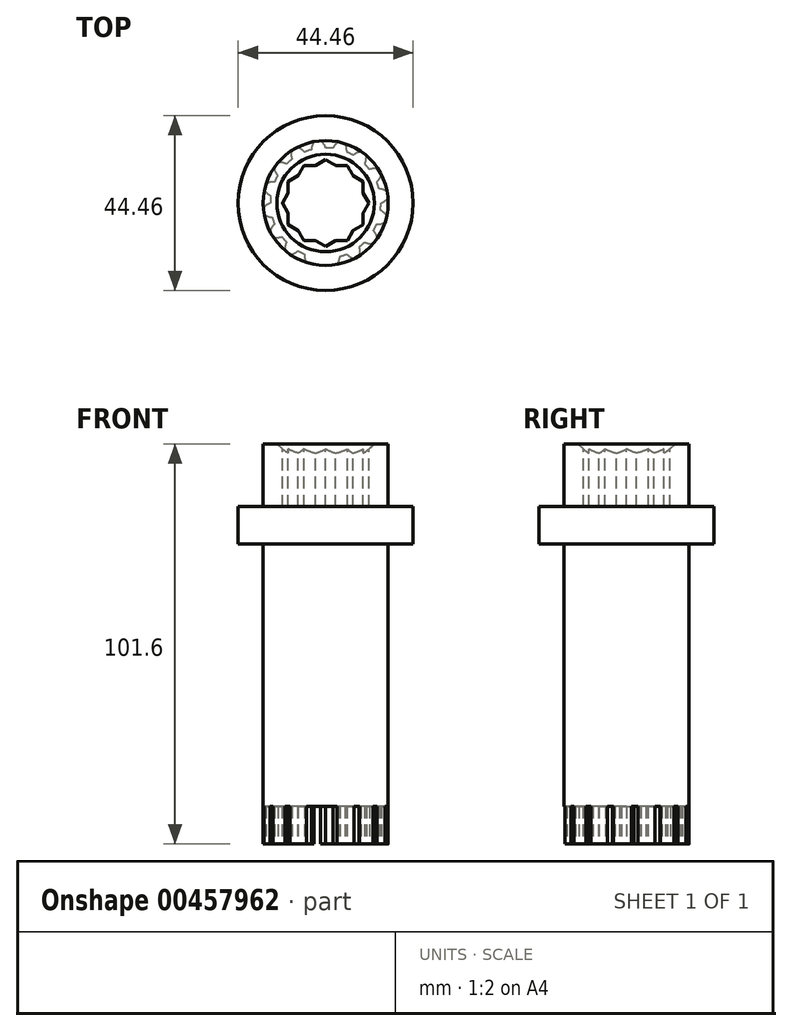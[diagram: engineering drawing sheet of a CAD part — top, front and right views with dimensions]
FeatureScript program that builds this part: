
annotation { "Feature Type Name" : "Feature", "Feature Type Description" : "" }
export const myFeature = defineFeature(function(context is Context, id is Id, definition is map)
    precondition{}
    {
        {
            var Q0;
            Q0=qCreatedBy(makeId("Front.planeOp"),FACE);
            var sketch = newSketch(context, id + "F0", { "sketchPlane" : qUnion([Q0])});
            skLineSegment(sketch, "E0", {"start": v(0, 0) * mm, "end": v(0, 64.52) * mm, "construction": true});
            skLineSegment(sketch, "E1", {"start": v(0, 101.6) * mm, "end": v(-15.88, 101.6) * mm});
            skLineSegment(sketch, "E2", {"start": v(-15.88, 101.6) * mm, "end": v(-15.88, 0) * mm});
            skLineSegment(sketch, "E3", {"start": v(-15.88, 0) * mm, "end": v(0, 0) * mm});
            skLineSegment(sketch, "E4", {"start": v(0, 101.6) * mm, "end": v(0, 0) * mm});
            skSolve(sketch);
        }
        {
            var Q0;
            Q0=qSketchRegion(id+"F0",true);
            var Q1;
            Q1=sQuery(id+"F0.wireOp",EDGE,"E4");
            revolve(context, id + "F1", {"entities" : qUnion([Q0]), "axis" : qUnion([Q1]), "revolveType" : RevolveType.FULL});
        }
        {
            var Q0;
            Q0=makeQuery(id+"F1.opRevolve","SWEPT_FACE",FACE,{"disambiguationData":[OSD([sQuery(id+"F0.wireOp",EDGE,"E3")])]});
            var sketch = newSketch(context, id + "F2", { "sketchPlane" : qUnion([Q0])});
            skCircle(sketch, "E5", {"center": v(0, 0) * mm, "radius": 15.87 * mm, "construction": true});
            skCircle(sketch, "E6", {"center": v(0, 0) * mm, "radius": 13.25 * mm, "construction": true});
            skCircle(sketch, "E7", {"center": v(0, 0) * mm, "radius": 14.03 * mm, "construction": true});
            skArc(sketch, "E8", {"start": v(1.24, 15.83) * mm, "mid": v(0.49, 15.02) * mm, "end": v(0, 14.03) * mm});
            skLineSegment(sketch, "E9", {"start": v(0, 14.03) * mm, "end": v(0, 17.07) * mm, "construction": true});
            skLineSegment(sketch, "E10", {"start": v(0, 0) * mm, "end": v(-1.3, 19.98) * mm, "construction": true});
            skArc(sketch, "E11.MirrorCS", {"start": v(-3.3, 15.53) * mm, "mid": v(-2.45, 14.83) * mm, "end": v(-1.83, 13.9) * mm});
            skArc(sketch, "E12", {"start": v(0, 14.03) * mm, "mid": v(-0.92, 14) * mm, "end": v(-1.83, 13.9) * mm});
            skArc(sketch, "E13.1.0", {"start": v(-8.99, 13.09) * mm, "mid": v(-7.93, 12.76) * mm, "end": v(-7.01, 12.15) * mm});
            skArc(sketch, "E13.1.2", {"start": v(-4.9, 15.1) * mm, "mid": v(-5.3, 14.06) * mm, "end": v(-5.37, 12.96) * mm});
            skArc(sketch, "E13.1.3", {"start": v(-5.37, 12.96) * mm, "mid": v(-6.2, 12.59) * mm, "end": v(-7.01, 12.15) * mm});
            skArc(sketch, "E13.2.0", {"start": v(-13.31, 8.65) * mm, "mid": v(-12.21, 8.75) * mm, "end": v(-11.13, 8.54) * mm});
            skArc(sketch, "E13.2.1", {"start": v(-10.31, 12.07) * mm, "mid": v(-12.13, 10.64) * mm, "end": v(-13.31, 8.65) * mm});
            skArc(sketch, "E13.2.2", {"start": v(-10.31, 12.07) * mm, "mid": v(-10.27, 10.97) * mm, "end": v(-9.92, 9.92) * mm});
            skArc(sketch, "E13.2.3", {"start": v(-9.92, 9.92) * mm, "mid": v(-10.55, 9.25) * mm, "end": v(-11.13, 8.54) * mm});
            skArc(sketch, "E13.3.0", {"start": v(-15.6, 2.9) * mm, "mid": v(-14.63, 3.41) * mm, "end": v(-13.55, 3.63) * mm});
            skArc(sketch, "E13.3.2", {"start": v(-14.15, 7.2) * mm, "mid": v(-13.69, 6.2) * mm, "end": v(-12.96, 5.37) * mm});
            skArc(sketch, "E13.3.3", {"start": v(-12.96, 5.37) * mm, "mid": v(-13.3, 4.51) * mm, "end": v(-13.55, 3.63) * mm});
            skArc(sketch, "E13.4.0", {"start": v(-15.53, -3.3) * mm, "mid": v(-14.83, -2.45) * mm, "end": v(-13.9, -1.83) * mm});
            skArc(sketch, "E13.4.2", {"start": v(-15.83, 1.24) * mm, "mid": v(-15.02, 0.49) * mm, "end": v(-14.03, 0) * mm});
            skArc(sketch, "E13.4.3", {"start": v(-14.03, 0) * mm, "mid": v(-14, -0.92) * mm, "end": v(-13.9, -1.83) * mm});
            skArc(sketch, "E13.5.0", {"start": v(-13.09, -8.99) * mm, "mid": v(-12.76, -7.93) * mm, "end": v(-12.15, -7.01) * mm});
            skArc(sketch, "E13.5.2", {"start": v(-15.1, -4.9) * mm, "mid": v(-14.06, -5.3) * mm, "end": v(-12.96, -5.37) * mm});
            skArc(sketch, "E13.5.3", {"start": v(-12.96, -5.37) * mm, "mid": v(-12.59, -6.2) * mm, "end": v(-12.15, -7.01) * mm});
            skArc(sketch, "E13.6.0", {"start": v(-8.65, -13.31) * mm, "mid": v(-8.75, -12.21) * mm, "end": v(-8.54, -11.13) * mm});
            skArc(sketch, "E13.6.2", {"start": v(-12.07, -10.31) * mm, "mid": v(-10.97, -10.27) * mm, "end": v(-9.92, -9.92) * mm});
            skArc(sketch, "E13.6.3", {"start": v(-9.92, -9.92) * mm, "mid": v(-9.25, -10.55) * mm, "end": v(-8.54, -11.13) * mm});
            skArc(sketch, "E13.7.0", {"start": v(-2.9, -15.6) * mm, "mid": v(-3.41, -14.63) * mm, "end": v(-3.63, -13.55) * mm});
            skArc(sketch, "E13.7.2", {"start": v(-7.2, -14.15) * mm, "mid": v(-6.2, -13.69) * mm, "end": v(-5.37, -12.96) * mm});
            skArc(sketch, "E13.7.3", {"start": v(-5.37, -12.96) * mm, "mid": v(-4.51, -13.3) * mm, "end": v(-3.63, -13.55) * mm});
            skArc(sketch, "E13.8.0", {"start": v(3.3, -15.53) * mm, "mid": v(2.45, -14.83) * mm, "end": v(1.83, -13.9) * mm});
            skArc(sketch, "E13.8.2", {"start": v(-1.24, -15.83) * mm, "mid": v(-0.49, -15.02) * mm, "end": v(0, -14.03) * mm});
            skArc(sketch, "E13.8.3", {"start": v(0, -14.03) * mm, "mid": v(0.92, -14) * mm, "end": v(1.83, -13.9) * mm});
            skArc(sketch, "E13.9.0", {"start": v(8.99, -13.09) * mm, "mid": v(7.93, -12.76) * mm, "end": v(7.01, -12.15) * mm});
            skArc(sketch, "E13.9.2", {"start": v(4.9, -15.1) * mm, "mid": v(5.3, -14.06) * mm, "end": v(5.37, -12.96) * mm});
            skArc(sketch, "E13.9.3", {"start": v(5.37, -12.96) * mm, "mid": v(6.2, -12.59) * mm, "end": v(7.01, -12.15) * mm});
            skArc(sketch, "E13.10.0", {"start": v(13.31, -8.65) * mm, "mid": v(12.21, -8.75) * mm, "end": v(11.13, -8.54) * mm});
            skArc(sketch, "E13.10.2", {"start": v(10.31, -12.07) * mm, "mid": v(10.27, -10.97) * mm, "end": v(9.92, -9.92) * mm});
            skArc(sketch, "E13.10.3", {"start": v(9.92, -9.92) * mm, "mid": v(10.55, -9.25) * mm, "end": v(11.13, -8.54) * mm});
            skArc(sketch, "E13.11.0", {"start": v(15.6, -2.9) * mm, "mid": v(14.63, -3.41) * mm, "end": v(13.55, -3.63) * mm});
            skArc(sketch, "E13.11.2", {"start": v(14.15, -7.2) * mm, "mid": v(13.69, -6.2) * mm, "end": v(12.96, -5.37) * mm});
            skArc(sketch, "E13.11.3", {"start": v(12.96, -5.37) * mm, "mid": v(13.3, -4.51) * mm, "end": v(13.55, -3.63) * mm});
            skArc(sketch, "E13.12.0", {"start": v(15.53, 3.3) * mm, "mid": v(14.83, 2.45) * mm, "end": v(13.9, 1.83) * mm});
            skArc(sketch, "E13.12.2", {"start": v(15.83, -1.24) * mm, "mid": v(15.02, -0.49) * mm, "end": v(14.03, 0) * mm});
            skArc(sketch, "E13.12.3", {"start": v(14.03, 0) * mm, "mid": v(14, 0.92) * mm, "end": v(13.9, 1.83) * mm});
            skArc(sketch, "E13.13.0", {"start": v(13.09, 8.99) * mm, "mid": v(12.76, 7.93) * mm, "end": v(12.15, 7.01) * mm});
            skArc(sketch, "E13.13.2", {"start": v(15.1, 4.9) * mm, "mid": v(14.06, 5.3) * mm, "end": v(12.96, 5.37) * mm});
            skArc(sketch, "E13.13.3", {"start": v(12.96, 5.37) * mm, "mid": v(12.59, 6.2) * mm, "end": v(12.15, 7.01) * mm});
            skArc(sketch, "E13.14.0", {"start": v(8.65, 13.31) * mm, "mid": v(8.75, 12.21) * mm, "end": v(8.54, 11.13) * mm});
            skArc(sketch, "E13.14.2", {"start": v(12.07, 10.31) * mm, "mid": v(10.97, 10.27) * mm, "end": v(9.92, 9.92) * mm});
            skArc(sketch, "E13.14.3", {"start": v(9.92, 9.92) * mm, "mid": v(9.25, 10.55) * mm, "end": v(8.54, 11.13) * mm});
            skArc(sketch, "E13.15.0", {"start": v(2.9, 15.6) * mm, "mid": v(3.41, 14.63) * mm, "end": v(3.63, 13.55) * mm});
            skArc(sketch, "E13.15.2", {"start": v(7.2, 14.15) * mm, "mid": v(6.2, 13.69) * mm, "end": v(5.37, 12.96) * mm});
            skArc(sketch, "E13.15.3", {"start": v(5.37, 12.96) * mm, "mid": v(4.51, 13.3) * mm, "end": v(3.63, 13.55) * mm});
            skCircle(sketch, "E14", {"center": v(0, 0) * mm, "radius": 18.28 * mm});
            skSolve(sketch);
        }
        {
            var Q0;
            Q0=makeQuery(id+"F1.opRevolve","SWEPT_FACE",FACE,{"disambiguationData":[OSD([sQuery(id+"F0.wireOp",EDGE,"E1")])]});
            var sketch = newSketch(context, id + "F3", { "sketchPlane" : qUnion([Q0])});
            skCircle(sketch, "E15.cCircle", {"center": v(0, 0) * mm, "radius": 9.53 * mm, "construction": true});
            skLineSegment(sketch, "E15.0", {"start": v(-5.5, 9.53) * mm, "end": v(5.5, 9.53) * mm, "construction": true});
            skLineSegment(sketch, "E15.1", {"start": v(5.5, 9.52) * mm, "end": v(11, 0) * mm, "construction": true});
            skLineSegment(sketch, "E15.2", {"start": v(11, 0) * mm, "end": v(5.5, -9.52) * mm, "construction": true});
            skLineSegment(sketch, "E15.3", {"start": v(5.5, -9.52) * mm, "end": v(-5.5, -9.53) * mm, "construction": true});
            skLineSegment(sketch, "E15.4", {"start": v(-5.5, -9.53) * mm, "end": v(-11, 0) * mm, "construction": true});
            skLineSegment(sketch, "E15.5", {"start": v(-11, 0) * mm, "end": v(-5.5, 9.52) * mm, "construction": true});
            skPoint(sketch, "E15.0.midPoint", {"position": v(0, 9.53) * mm});
            skLineSegment(sketch, "E16.0", {"start": v(9.53, 5.5) * mm, "end": v(9.53, -5.5) * mm, "construction": true});
            skLineSegment(sketch, "E16.1", {"start": v(9.52, -5.5) * mm, "end": v(0, -11) * mm, "construction": true});
            skLineSegment(sketch, "E16.2", {"start": v(0, -11) * mm, "end": v(-9.52, -5.5) * mm, "construction": true});
            skLineSegment(sketch, "E16.3", {"start": v(-9.52, -5.5) * mm, "end": v(-9.53, 5.5) * mm, "construction": true});
            skLineSegment(sketch, "E16.4", {"start": v(-9.53, 5.5) * mm, "end": v(0, 11) * mm, "construction": true});
            skLineSegment(sketch, "E16.5", {"start": v(0, 11) * mm, "end": v(9.52, 5.5) * mm, "construction": true});
            skPoint(sketch, "E16.0.midPoint", {"position": v(9.53, 0) * mm});
            skLineSegment(sketch, "E17", {"start": v(-5.5, 9.53) * mm, "end": v(-2.55, 9.53) * mm});
            skLineSegment(sketch, "E18", {"start": v(-2.55, 9.53) * mm, "end": v(0, 11) * mm});
            skLineSegment(sketch, "E19", {"start": v(0, 11) * mm, "end": v(2.55, 9.53) * mm});
            skLineSegment(sketch, "E20", {"start": v(2.55, 9.53) * mm, "end": v(5.5, 9.53) * mm});
            skLineSegment(sketch, "E21", {"start": v(5.5, 9.53) * mm, "end": v(6.97, 6.97) * mm});
            skLineSegment(sketch, "E22", {"start": v(6.97, 6.97) * mm, "end": v(9.53, 5.5) * mm});
            skLineSegment(sketch, "E23", {"start": v(9.53, 2.55) * mm, "end": v(11, 0) * mm});
            skLineSegment(sketch, "E24", {"start": v(11, 0) * mm, "end": v(9.53, -2.55) * mm});
            skLineSegment(sketch, "E25", {"start": v(9.53, -2.55) * mm, "end": v(9.53, -5.5) * mm});
            skLineSegment(sketch, "E26", {"start": v(9.53, -5.5) * mm, "end": v(6.97, -6.97) * mm});
            skLineSegment(sketch, "E27", {"start": v(6.97, -6.97) * mm, "end": v(5.5, -9.52) * mm});
            skLineSegment(sketch, "E28", {"start": v(2.55, -9.53) * mm, "end": v(0, -11) * mm});
            skLineSegment(sketch, "E29", {"start": v(-2.55, -9.53) * mm, "end": v(-5.5, -9.53) * mm});
            skLineSegment(sketch, "E30", {"start": v(-6.97, -6.97) * mm, "end": v(-9.52, -5.5) * mm});
            skLineSegment(sketch, "E31", {"start": v(-9.53, -2.55) * mm, "end": v(-11, 0) * mm});
            skLineSegment(sketch, "E32", {"start": v(-9.52, -5.5) * mm, "end": v(-9.53, -2.55) * mm});
            skLineSegment(sketch, "E33", {"start": v(-5.5, -9.53) * mm, "end": v(-6.97, -6.97) * mm});
            skLineSegment(sketch, "E34", {"start": v(0, -11) * mm, "end": v(-2.55, -9.53) * mm});
            skLineSegment(sketch, "E35", {"start": v(5.5, -9.52) * mm, "end": v(2.55, -9.53) * mm});
            skLineSegment(sketch, "E36", {"start": v(9.53, 5.5) * mm, "end": v(9.53, 2.55) * mm});
            skLineSegment(sketch, "E37", {"start": v(-5.5, 9.53) * mm, "end": v(-6.97, 6.97) * mm});
            skLineSegment(sketch, "E38", {"start": v(-6.97, 6.97) * mm, "end": v(-9.53, 5.5) * mm});
            skLineSegment(sketch, "E39", {"start": v(-9.53, 5.5) * mm, "end": v(-9.53, 2.55) * mm});
            skLineSegment(sketch, "E40", {"start": v(-9.53, 2.55) * mm, "end": v(-11, 0) * mm});
            skSolve(sketch);
        }
        {
            var Q0;
            Q0=qSketchRegion(id+"F3",true);
            extrude(context, id + "F4", {"entities" : qUnion([Q0]), "operationType" : NewBodyOperationType.REMOVE, "oppositeDirection" : true, "depth" : 19.05 * mm});
        }
        {
            var Q0;
            Q0=qCreatedBy(makeId("Front.planeOp"),FACE);
            var sketch = newSketch(context, id + "F5", { "sketchPlane" : qUnion([Q0])});
            skLineSegment(sketch, "E41", {"start": v(-15.88, 104.78) * mm, "end": v(-8.9, 98.43) * mm});
            skLineSegment(sketch, "E42", {"start": v(-8.9, 98.43) * mm, "end": v(0, 98.43) * mm});
            skLineSegment(sketch, "E43", {"start": v(0, 98.43) * mm, "end": v(0, 104.78) * mm});
            skLineSegment(sketch, "E44", {"start": v(0, 104.78) * mm, "end": v(-15.88, 104.78) * mm});
            skSolve(sketch);
        }
        {
            var Q0;
            Q0=qSketchRegion(id+"F5",true);
            var Q1;
            Q1=sQuery(id+"F5.wireOp",EDGE,"E43");
            revolve(context, id + "F6", {"operationType" : NewBodyOperationType.REMOVE, "entities" : qUnion([Q0]), "axis" : qUnion([Q1]), "revolveType" : RevolveType.FULL, "oppositeDirection" : true});
        }
        {
            var Q0;
            {var subQ0=sQuery(id+"F2.wireOp",EDGE,"E8");Q0=makeQuery(id+"F2.imprint","IMPRINT",FACE,{"disambiguationData":[TD([[makeQuery(id+"F2.imprint","IMPRINT",EDGE,{"derivedFrom":subQ0}),-1.0]])]});}
            var Q1;
            {var subQ0=sQuery(id+"F2.wireOp",EDGE,"E13.1.0");Q1=makeQuery(id+"F2.imprint","IMPRINT",FACE,{"disambiguationData":[TD([[makeQuery(id+"F2.imprint","IMPRINT",EDGE,{"derivedFrom":subQ0}),1.0]])]});}
            var Q2;
            {var subQ0=sQuery(id+"F2.wireOp",EDGE,"E13.2.0");Q2=makeQuery(id+"F2.imprint","IMPRINT",FACE,{"disambiguationData":[TD([[makeQuery(id+"F2.imprint","IMPRINT",EDGE,{"derivedFrom":subQ0}),1.0]])]});}
            var Q3;
            {var subQ0=sQuery(id+"F2.wireOp",EDGE,"E13.3.0");Q3=makeQuery(id+"F2.imprint","IMPRINT",FACE,{"disambiguationData":[TD([[makeQuery(id+"F2.imprint","IMPRINT",EDGE,{"derivedFrom":subQ0}),1.0]])]});}
            var Q4;
            {var subQ0=sQuery(id+"F2.wireOp",EDGE,"E13.4.0");Q4=makeQuery(id+"F2.imprint","IMPRINT",FACE,{"disambiguationData":[TD([[makeQuery(id+"F2.imprint","IMPRINT",EDGE,{"derivedFrom":subQ0}),1.0]])]});}
            var Q5;
            {var subQ0=sQuery(id+"F2.wireOp",EDGE,"E13.5.0");Q5=makeQuery(id+"F2.imprint","IMPRINT",FACE,{"disambiguationData":[TD([[makeQuery(id+"F2.imprint","IMPRINT",EDGE,{"derivedFrom":subQ0}),1.0]])]});}
            var Q6;
            {var subQ0=sQuery(id+"F2.wireOp",EDGE,"E13.6.0");Q6=makeQuery(id+"F2.imprint","IMPRINT",FACE,{"disambiguationData":[TD([[makeQuery(id+"F2.imprint","IMPRINT",EDGE,{"derivedFrom":subQ0}),1.0]])]});}
            var Q7;
            {var subQ0=sQuery(id+"F2.wireOp",EDGE,"E13.7.0");Q7=makeQuery(id+"F2.imprint","IMPRINT",FACE,{"disambiguationData":[TD([[makeQuery(id+"F2.imprint","IMPRINT",EDGE,{"derivedFrom":subQ0}),1.0]])]});}
            var Q8;
            {var subQ0=sQuery(id+"F2.wireOp",EDGE,"E13.8.0");Q8=makeQuery(id+"F2.imprint","IMPRINT",FACE,{"disambiguationData":[TD([[makeQuery(id+"F2.imprint","IMPRINT",EDGE,{"derivedFrom":subQ0}),1.0]])]});}
            var Q9;
            {var subQ0=sQuery(id+"F2.wireOp",EDGE,"E13.9.0");Q9=makeQuery(id+"F2.imprint","IMPRINT",FACE,{"disambiguationData":[TD([[makeQuery(id+"F2.imprint","IMPRINT",EDGE,{"derivedFrom":subQ0}),1.0]])]});}
            var Q10;
            {var subQ0=sQuery(id+"F2.wireOp",EDGE,"E13.10.0");Q10=makeQuery(id+"F2.imprint","IMPRINT",FACE,{"disambiguationData":[TD([[makeQuery(id+"F2.imprint","IMPRINT",EDGE,{"derivedFrom":subQ0}),1.0]])]});}
            var Q11;
            {var subQ0=sQuery(id+"F2.wireOp",EDGE,"E13.11.0");Q11=makeQuery(id+"F2.imprint","IMPRINT",FACE,{"disambiguationData":[TD([[makeQuery(id+"F2.imprint","IMPRINT",EDGE,{"derivedFrom":subQ0}),1.0]])]});}
            var Q12;
            {var subQ0=sQuery(id+"F2.wireOp",EDGE,"E13.12.0");Q12=makeQuery(id+"F2.imprint","IMPRINT",FACE,{"disambiguationData":[TD([[makeQuery(id+"F2.imprint","IMPRINT",EDGE,{"derivedFrom":subQ0}),1.0]])]});}
            var Q13;
            {var subQ0=sQuery(id+"F2.wireOp",EDGE,"E13.13.0");Q13=makeQuery(id+"F2.imprint","IMPRINT",FACE,{"disambiguationData":[TD([[makeQuery(id+"F2.imprint","IMPRINT",EDGE,{"derivedFrom":subQ0}),1.0]])]});}
            var Q14;
            {var subQ0=sQuery(id+"F2.wireOp",EDGE,"E13.14.0");Q14=makeQuery(id+"F2.imprint","IMPRINT",FACE,{"disambiguationData":[TD([[makeQuery(id+"F2.imprint","IMPRINT",EDGE,{"derivedFrom":subQ0}),1.0]])]});}
            var Q15;
            {var subQ0=sQuery(id+"F2.wireOp",EDGE,"E13.15.0");Q15=makeQuery(id+"F2.imprint","IMPRINT",FACE,{"disambiguationData":[TD([[makeQuery(id+"F2.imprint","IMPRINT",EDGE,{"derivedFrom":subQ0}),1.0]])]});}
            extrude(context, id + "F7", {"entities" : qUnion([Q0, Q1, Q2, Q3, Q4, Q5, Q6, Q7, Q8, Q9, Q10, Q11, Q12, Q13, Q14, Q15]), "operationType" : NewBodyOperationType.REMOVE, "oppositeDirection" : true, "depth" : 9.52 * mm});
        }
        {
            var Q0;
            Q0=qCreatedBy(makeId("Front.planeOp"),FACE);
            var sketch = newSketch(context, id + "F8", { "sketchPlane" : qUnion([Q0])});
            skLineSegment(sketch, "E45", {"start": v(0, 0) * mm, "end": v(0, 110.4) * mm, "construction": true});
            skLineSegment(sketch, "E46.bottom", {"start": v(-22.23, 85.73) * mm, "end": v(0, 85.73) * mm});
            skLineSegment(sketch, "E46.top", {"start": v(-22.23, 76.2) * mm, "end": v(0, 76.2) * mm});
            skLineSegment(sketch, "E46.left", {"start": v(-22.23, 85.73) * mm, "end": v(-22.23, 76.2) * mm});
            skLineSegment(sketch, "E46.right", {"start": v(0, 85.73) * mm, "end": v(0, 76.2) * mm});
            skSolve(sketch);
        }
        {
            var Q0;
            Q0 = qSketchRegion(id + "F8", true);
            var Q1;
            Q1=sQuery(id+"F8.wireOp",EDGE,"E45");
            revolve(context, id + "F9", {"operationType" : NewBodyOperationType.ADD, "entities" : qUnion([Q0]), "axis" : qUnion([Q1]), "revolveType" : RevolveType.FULL});
        }
    });
